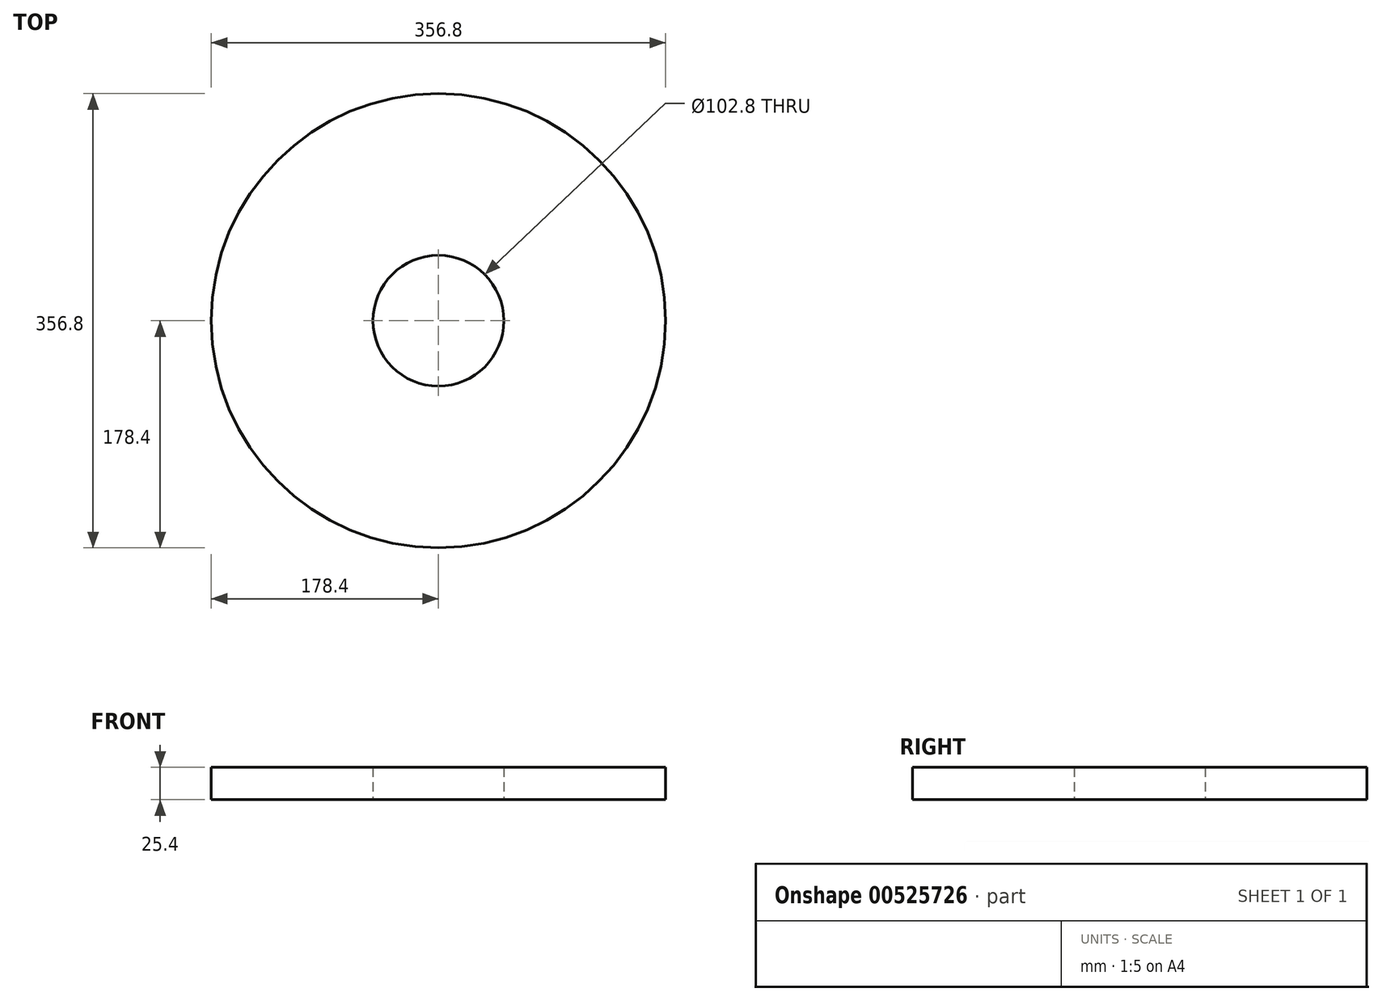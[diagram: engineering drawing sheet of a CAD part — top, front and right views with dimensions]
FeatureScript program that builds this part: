
annotation { "Feature Type Name" : "Feature", "Feature Type Description" : "" }
export const myFeature = defineFeature(function(context is Context, id is Id, definition is map)
    precondition{}
    {
        {
            var Q0;
            Q0=qCreatedBy(makeId("Top.planeOp"),FACE);
            var sketch = newSketch(context, id + "F0", { "sketchPlane" : qUnion([Q0])});
            skCircle(sketch, "E0", {"center": v(0, 0) * mm, "radius": 51.4 * mm});
            skCircle(sketch, "E1", {"center": v(0, 0) * mm, "radius": 178.4 * mm});
            skSolve(sketch);
        }
        {
            var Q0;
            Q0 = qSketchRegion(id + "F0", true);
            extrude(context, id + "F1", {"entities" : qUnion([Q0]), "depth" : 25.4 * mm, "offsetDistance" : 25.4 * mm});
        }
    });
